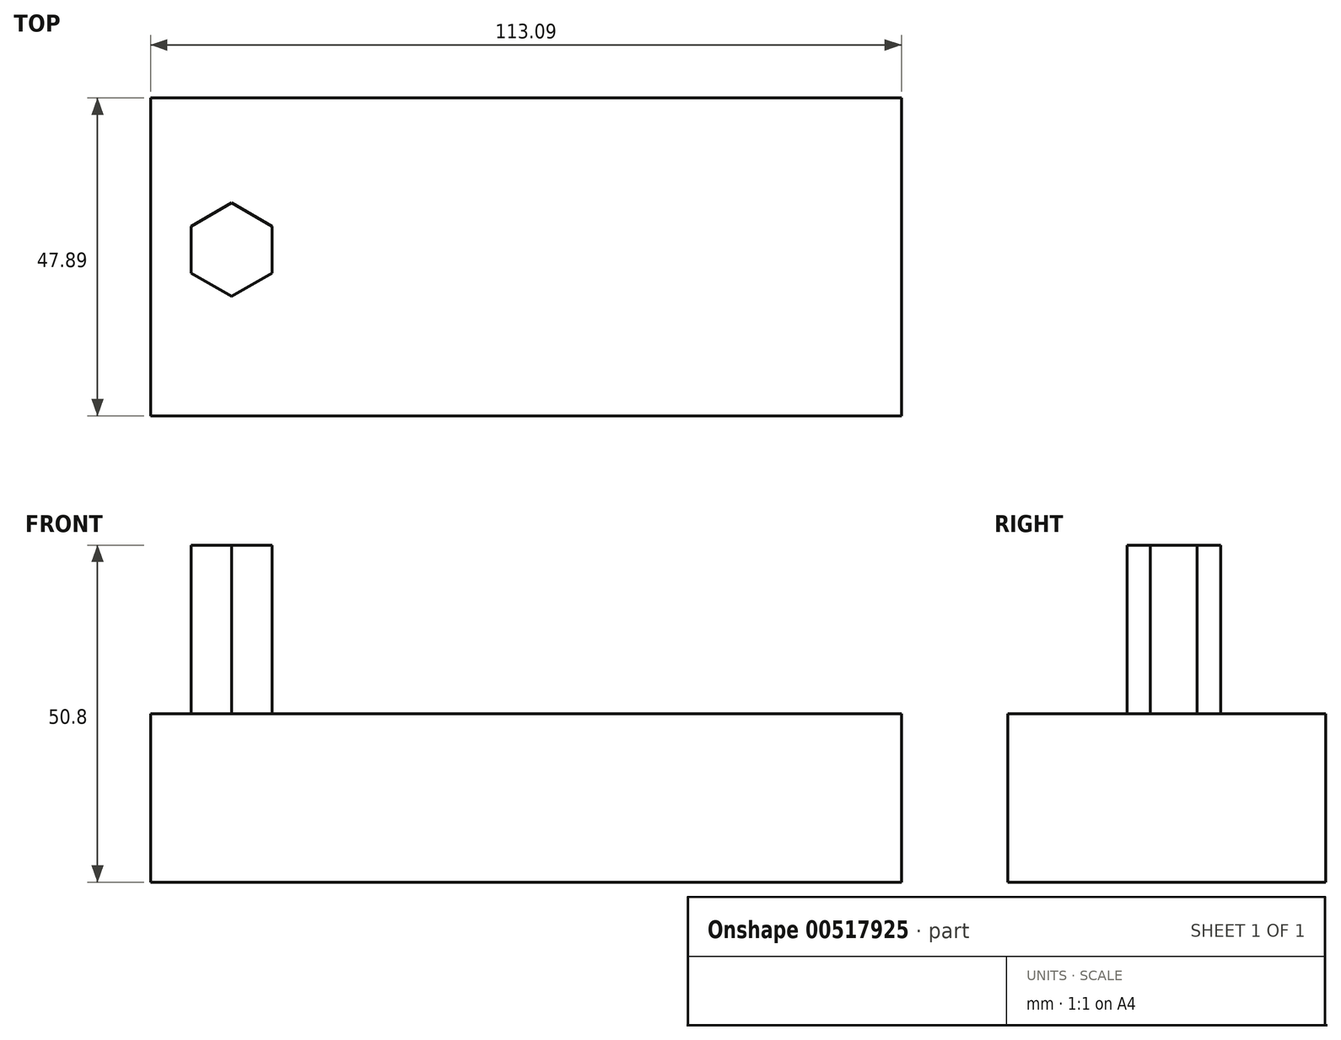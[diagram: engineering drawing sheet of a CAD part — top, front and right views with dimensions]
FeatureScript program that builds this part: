
annotation { "Feature Type Name" : "Feature", "Feature Type Description" : "" }
export const myFeature = defineFeature(function(context is Context, id is Id, definition is map)
    precondition{}
    {
        {
            var Q0;
            Q0=qCreatedBy(makeId("Top.planeOp"),FACE);
            var sketch = newSketch(context, id + "F0", { "sketchPlane" : qUnion([Q0])});
            skLineSegment(sketch, "E0.bottom", {"start": v(-65.98, 22.85) * mm, "end": v(47.1, 22.85) * mm});
            skLineSegment(sketch, "E0.top", {"start": v(-65.98, -25.04) * mm, "end": v(47.1, -25.04) * mm});
            skLineSegment(sketch, "E0.left", {"start": v(-65.98, 22.85) * mm, "end": v(-65.98, -25.04) * mm});
            skLineSegment(sketch, "E0.right", {"start": v(47.1, 22.85) * mm, "end": v(47.1, -25.04) * mm});
            skSolve(sketch);
        }
        {
            var Q0;
            Q0 = qSketchRegion(id + "F0", true);
            extrude(context, id + "F1", {"entities" : qUnion([Q0]), "depth" : 25.4 * mm, "offsetDistance" : 25.4 * mm});
        }
        {
            var Q0;
            Q0=makeQuery(id+"F1.opExtrude","CAP_FACE",FACE,{"disambiguationData":[OSD([sQuery(id+"F0.wireOp",EDGE,"E0.bottom"),sQuery(id+"F0.wireOp",EDGE,"E0.top"),sQuery(id+"F0.wireOp",EDGE,"E0.left"),sQuery(id+"F0.wireOp",EDGE,"E0.right")])],"isStart":false});
            var sketch = newSketch(context, id + "F2", { "sketchPlane" : qUnion([Q0])});
            skCircle(sketch, "E1.cCircle", {"center": v(-53.76, 0) * mm, "radius": 6.1 * mm, "construction": true});
            skLineSegment(sketch, "E1.0", {"start": v(-47.65, 3.53) * mm, "end": v(-47.65, -3.53) * mm});
            skLineSegment(sketch, "E1.1", {"start": v(-47.65, -3.53) * mm, "end": v(-53.76, -7.05) * mm});
            skLineSegment(sketch, "E1.2", {"start": v(-53.76, -7.05) * mm, "end": v(-59.86, -3.53) * mm});
            skLineSegment(sketch, "E1.3", {"start": v(-59.86, -3.53) * mm, "end": v(-59.86, 3.53) * mm});
            skLineSegment(sketch, "E1.4", {"start": v(-59.86, 3.53) * mm, "end": v(-53.76, 7.05) * mm});
            skLineSegment(sketch, "E1.5", {"start": v(-53.76, 7.05) * mm, "end": v(-47.65, 3.53) * mm});
            skPoint(sketch, "E1.0.midPoint", {"position": v(-47.65, 0) * mm});
            skSolve(sketch);
        }
        {
            var Q0;
            Q0=makeQuery(id+"F2.imprint","IMPRINT",FACE,{"disambiguationData":[TD([[makeQuery(id+"F2.imprint","IMPRINT",EDGE,{"derivedFrom":sQuery(id+"F2.wireOp",EDGE,"E1.0")}),-1.0]])]});
            extrude(context, id + "F3", {"entities" : qUnion([Q0]), "operationType" : NewBodyOperationType.ADD, "depth" : 25.4 * mm, "offsetDistance" : 25.4 * mm});
        }
    });
